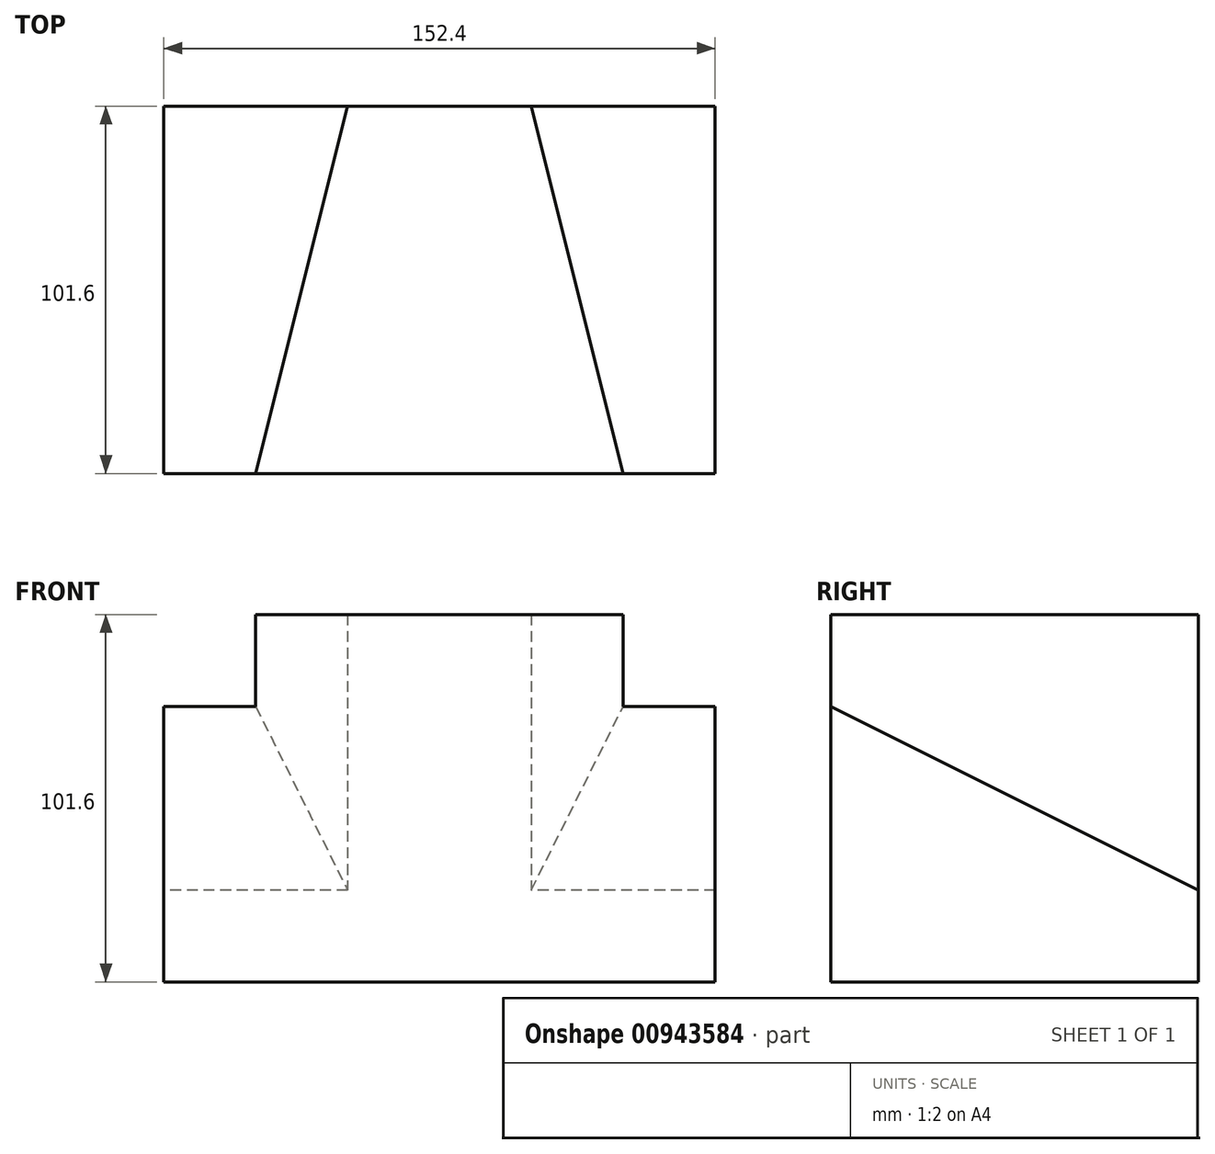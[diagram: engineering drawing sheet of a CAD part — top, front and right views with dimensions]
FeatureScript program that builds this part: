
annotation { "Feature Type Name" : "Feature", "Feature Type Description" : "" }
export const myFeature = defineFeature(function(context is Context, id is Id, definition is map)
    precondition{}
    {
        {
            var Q0;
            Q0=qCreatedBy(makeId("Top.planeOp"),FACE);
            var sketch = newSketch(context, id + "F0", { "sketchPlane" : qUnion([Q0])});
            skLineSegment(sketch, "E0.bottom", {"start": v(0, 0) * mm, "end": v(152.4, 0) * mm});
            skLineSegment(sketch, "E0.top", {"start": v(0, 101.6) * mm, "end": v(152.4, 101.6) * mm});
            skLineSegment(sketch, "E0.left", {"start": v(0, 0) * mm, "end": v(0, 101.6) * mm});
            skLineSegment(sketch, "E0.right", {"start": v(152.4, 0) * mm, "end": v(152.4, 101.6) * mm});
            skSolve(sketch);
        }
        {
            var Q0;
            Q0 = qSketchRegion(id + "F0", true);
            extrude(context, id + "F1", {"entities" : qUnion([Q0]), "depth" : 76.2 * mm, "offsetDistance" : 25.4 * mm});
        }
        {
            var Q0;
            Q0=makeQuery(id+"F1.opExtrude","SWEPT_FACE",FACE,{"disambiguationData":[OSD([sQuery(id+"F0.wireOp",EDGE,"E0.left")])]});
            var sketch = newSketch(context, id + "F2", { "sketchPlane" : qUnion([Q0])});
            skLineSegment(sketch, "E1", {"start": v(0, 76.2) * mm, "end": v(-101.6, 25.4) * mm});
            skSolve(sketch);
        }
        {
            var Q0;
            Q0 = qSketchRegion(id + "F2", true);
            var Q1;
            {var subQ0=sQuery(id+"F2.wireOp",EDGE,"E1");Q1=makeQuery(id+"F2.imprint","IMPRINT",FACE,{"disambiguationData":[TD([[makeQuery(id+"F2.imprint","IMPRINT",EDGE,{"derivedFrom":subQ0}),-1.0]])]});}
            extrude(context, id + "F3", {"entities" : qUnion([Q0, Q1]), "operationType" : NewBodyOperationType.REMOVE, "endBound" : BoundingType.THROUGH_ALL, "oppositeDirection" : true, "depth" : 25.4 * mm, "offsetDistance" : 25.4 * mm});
        }
        {
            var Q0;
            Q0=makeQuery(id+"F3.boolean.opBoolean","COPY",FACE,{"derivedFrom":makeQuery(id+"F3.opExtrude","SWEPT_FACE",FACE,{"disambiguationData":[OSD([sQuery(id+"F2.wireOp",EDGE,"E1")])]})});
            var sketch = newSketch(context, id + "F4", { "sketchPlane" : qUnion([Q0])});
            skLineSegment(sketch, "E2", {"start": v(25.4, -34.08) * mm, "end": v(50.8, 79.51) * mm});
            skLineSegment(sketch, "E3", {"start": v(101.6, 79.51) * mm, "end": v(127, -34.08) * mm});
            skLineSegment(sketch, "E4", {"start": v(127, -34.08) * mm, "end": v(25.4, -34.08) * mm});
            skLineSegment(sketch, "E5", {"start": v(101.6, 79.51) * mm, "end": v(50.8, 79.51) * mm});
            skSolve(sketch);
        }
        {
            var Q0;
            Q0=qCreatedBy(makeId("Top.planeOp"),FACE);
            cPlane(context, id + "F5", {"entities" : qUnion([Q0]), "cplaneType" : CPlaneType.OFFSET, "offset" : 101.6 * mm, "width" : 152.4 * mm, "height" : 152.4 * mm});
        }
        {
            var Q0;
            Q0=qCreatedBy(id+"F5.planeOp",FACE);
            var sketch = newSketch(context, id + "F6", { "sketchPlane" : qUnion([Q0])});
            skLineSegment(sketch, "E6", {"start": v(50.8, 101.6) * mm, "end": v(25.4, 0) * mm});
            skLineSegment(sketch, "E7", {"start": v(101.6, 101.6) * mm, "end": v(127, 0) * mm});
            skLineSegment(sketch, "E8", {"start": v(127, 0) * mm, "end": v(25.4, 0) * mm});
            skLineSegment(sketch, "E9", {"start": v(101.6, 101.6) * mm, "end": v(50.8, 101.6) * mm});
            skSolve(sketch);
        }
        {
            var Q0;
            Q0 = qSketchRegion(id + "F6", true);
            var Q1;
            Q1 = qSketchRegion(id + "F4", true);
            loft(context, id + "F7", {"operationType" : NewBodyOperationType.ADD, "sheetProfilesArray" : [{ "sheetProfileEntities" : qUnion([Q0]) }, { "sheetProfileEntities" : qUnion([Q1]) }]});
        }
    });
